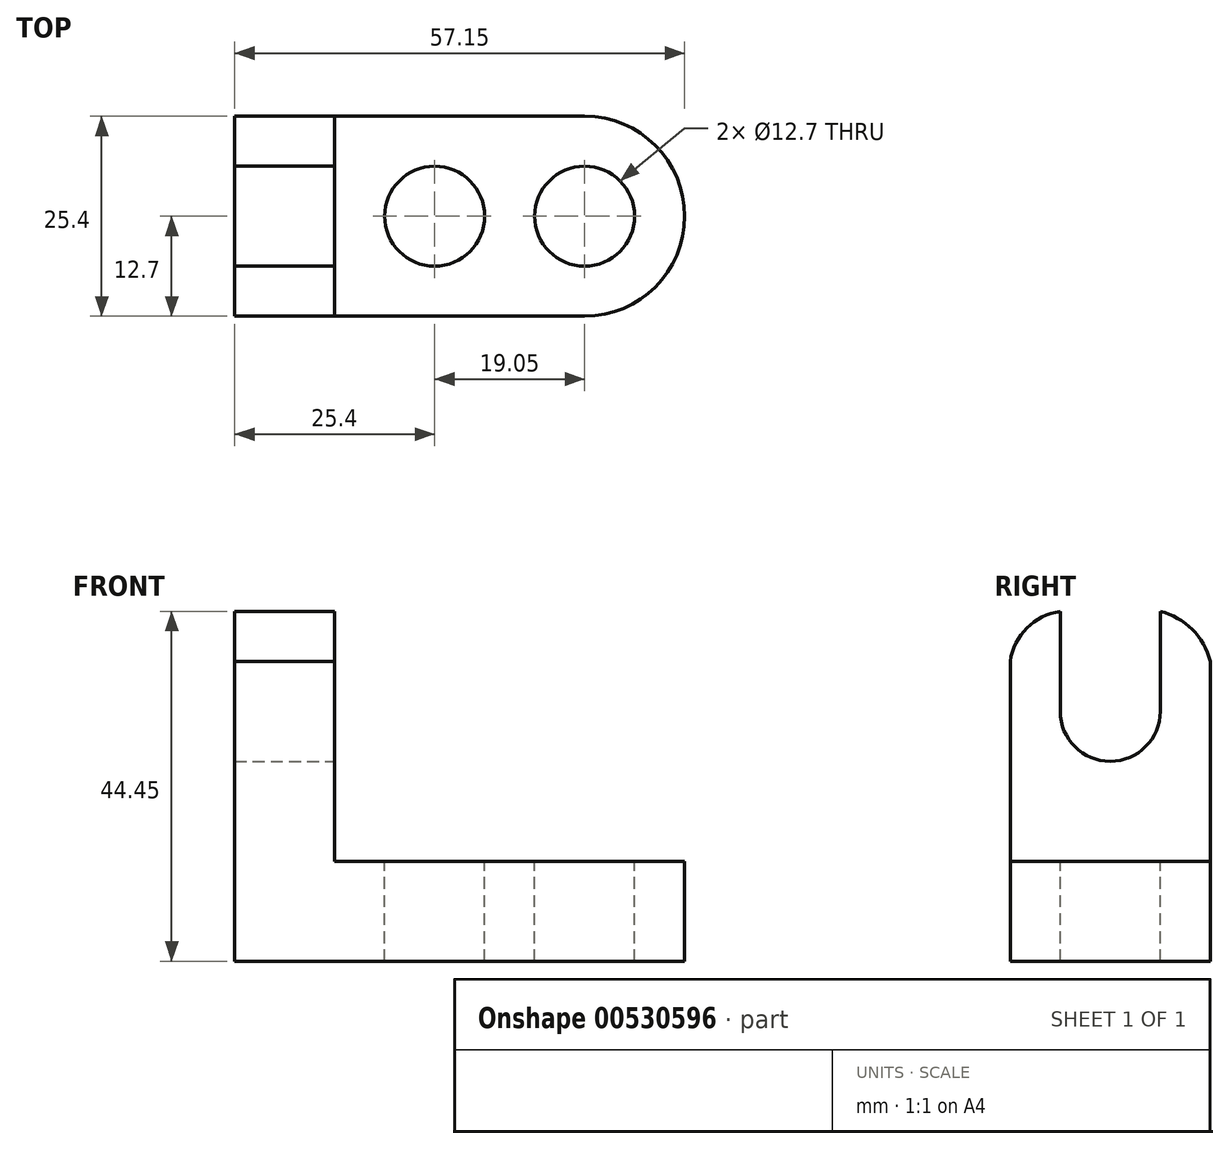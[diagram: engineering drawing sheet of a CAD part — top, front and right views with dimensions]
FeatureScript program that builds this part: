
annotation { "Feature Type Name" : "Feature", "Feature Type Description" : "" }
export const myFeature = defineFeature(function(context is Context, id is Id, definition is map)
    precondition{}
    {
        {
            var Q0;
            Q0=qCreatedBy(makeId("Front.planeOp"),FACE);
            var sketch = newSketch(context, id + "F0", { "sketchPlane" : qUnion([Q0])});
            skLineSegment(sketch, "E0", {"start": v(0, 0) * mm, "end": v(-44.45, 0) * mm});
            skLineSegment(sketch, "E1", {"start": v(-44.45, 0) * mm, "end": v(-44.45, 12.7) * mm});
            skLineSegment(sketch, "E2", {"start": v(-44.45, 12.7) * mm, "end": v(0, 12.7) * mm});
            skLineSegment(sketch, "E3", {"start": v(0, 12.7) * mm, "end": v(0, 0) * mm});
            skSolve(sketch);
        }
        {
            var Q0;
            Q0 = qSketchRegion(id + "F0", true);
            extrude(context, id + "F1", {"entities" : qUnion([Q0]), "depth" : 25.4 * mm, "offsetDistance" : 25.4 * mm});
        }
        {
            var Q0;
            Q0=makeQuery(id+"F1.opExtrude","SWEPT_FACE",FACE,{"disambiguationData":[OSD([sQuery(id+"F0.wireOp",EDGE,"E2")])]});
            var sketch = newSketch(context, id + "F2", { "sketchPlane" : qUnion([Q0])});
            skArc(sketch, "E4", {"start": v(0, -25.4) * mm, "mid": v(12.7, -12.7) * mm, "end": v(0, 0) * mm});
            skSolve(sketch);
        }
        {
            var Q0;
            Q0 = qSketchRegion(id + "F2", true);
            var Q1;
            Q1=makeQuery(id+"F2.imprint","IMPRINT",FACE,{"disambiguationData":[TD([[makeQuery(id+"F2.imprint","IMPRINT",EDGE,{"derivedFrom":sQuery(id+"F2.wireOp",EDGE,"E4")}),1.0]])]});
            extrude(context, id + "F3", {"entities" : qUnion([Q0, Q1]), "operationType" : NewBodyOperationType.ADD, "oppositeDirection" : true, "depth" : 12.7 * mm, "offsetDistance" : 25.4 * mm});
        }
        {
            var Q0;
            {var subQ0=sQuery(id+"F0.wireOp",EDGE,"E2");Q0=makeQuery(id+"F3.boolean.opBoolean","MERGE",FACE,{"derivedFrom":[makeQuery(id+"F1.opExtrude","SWEPT_FACE",FACE,{"disambiguationData":[OSD([subQ0])]}),makeQuery(id+"F3.opExtrude","CAP_FACE",FACE,{"disambiguationData":[OSD([subQ0,sQuery(id+"F0.wireOp",EDGE,"E3"),sQuery(id+"F2.wireOp",EDGE,"E4")])],"isStart":true})]});}
            var sketch = newSketch(context, id + "F4", { "sketchPlane" : qUnion([Q0])});
            skLineSegment(sketch, "E5", {"start": v(-44.45, 0) * mm, "end": v(-31.75, 0) * mm});
            skLineSegment(sketch, "E6", {"start": v(-31.75, 0) * mm, "end": v(-31.75, -25.4) * mm});
            skLineSegment(sketch, "E7", {"start": v(-31.75, -25.4) * mm, "end": v(-44.45, -25.4) * mm});
            skLineSegment(sketch, "E8", {"start": v(-44.45, -25.4) * mm, "end": v(-44.45, 0) * mm});
            skSolve(sketch);
        }
        {
            var Q0;
            Q0=makeQuery(id+"F4.imprint","IMPRINT",FACE,{"disambiguationData":[TD([[makeQuery(id+"F4.imprint","IMPRINT",EDGE,{"derivedFrom":sQuery(id+"F4.wireOp",EDGE,"E5")}),-1.0]])]});
            extrude(context, id + "F5", {"entities" : qUnion([Q0]), "operationType" : NewBodyOperationType.ADD, "depth" : 31.75 * mm, "offsetDistance" : 25.4 * mm});
        }
        {
            var Q0;
            Q0=makeQuery(id+"F5.opExtrude","SWEPT_FACE",FACE,{"disambiguationData":[OSD([sQuery(id+"F4.wireOp",EDGE,"E6")])]});
            var sketch = newSketch(context, id + "F6", { "sketchPlane" : qUnion([Q0])});
            skArc(sketch, "E9", {"start": v(-19.05, 44.45) * mm, "mid": v(-23.29, 42.34) * mm, "end": v(-25.4, 38.1) * mm});
            skArc(sketch, "E10", {"start": v(0, 38.1) * mm, "mid": v(-2.28, 42.17) * mm, "end": v(-6.35, 44.45) * mm});
            skSolve(sketch);
        }
        {
            var Q0;
            Q0 = qSketchRegion(id + "F6", true);
            var Q1;
            {var subQ0=sQuery(id+"F6.wireOp",EDGE,"E9");Q1=makeQuery(id+"F6.imprint","IMPRINT",FACE,{"disambiguationData":[TD([[makeQuery(id+"F6.imprint","IMPRINT",EDGE,{"derivedFrom":subQ0}),-1.0]])]});}
            var Q2;
            {var subQ0=sQuery(id+"F6.wireOp",EDGE,"E10");Q2=makeQuery(id+"F6.imprint","IMPRINT",FACE,{"disambiguationData":[TD([[makeQuery(id+"F6.imprint","IMPRINT",EDGE,{"derivedFrom":subQ0}),-1.0]])]});}
            extrude(context, id + "F7", {"entities" : qUnion([Q0, Q1, Q2]), "operationType" : NewBodyOperationType.REMOVE, "oppositeDirection" : true, "depth" : 25.4 * mm, "offsetDistance" : 25.4 * mm});
        }
        {
            var Q0;
            Q0=makeQuery(id+"F5.opExtrude","SWEPT_FACE",FACE,{"disambiguationData":[OSD([sQuery(id+"F4.wireOp",EDGE,"E6")])]});
            var sketch = newSketch(context, id + "F8", { "sketchPlane" : qUnion([Q0])});
            skLineSegment(sketch, "E11", {"start": v(-19.05, 44.45) * mm, "end": v(-19.05, 31.75) * mm});
            skLineSegment(sketch, "E12", {"start": v(-19.05, 31.75) * mm, "end": v(-6.35, 31.75) * mm});
            skLineSegment(sketch, "E13", {"start": v(-6.35, 31.75) * mm, "end": v(-6.35, 44.45) * mm});
            skLineSegment(sketch, "E14", {"start": v(-6.35, 44.45) * mm, "end": v(-19.05, 44.45) * mm});
            skArc(sketch, "E15", {"start": v(-19.05, 31.75) * mm, "mid": v(-12.7, 25.4) * mm, "end": v(-6.35, 31.75) * mm});
            skSolve(sketch);
        }
        {
            var Q0;
            Q0 = qSketchRegion(id + "F8", true);
            extrude(context, id + "F9", {"entities" : qUnion([Q0]), "operationType" : NewBodyOperationType.REMOVE, "oppositeDirection" : true, "depth" : 25.4 * mm, "offsetDistance" : 25.4 * mm});
        }
        {
            var Q0;
            {var subQ0=sQuery(id+"F0.wireOp",EDGE,"E2");Q0=makeQuery(id+"F3.boolean.opBoolean","MERGE",FACE,{"derivedFrom":[makeQuery(id+"F1.opExtrude","SWEPT_FACE",FACE,{"disambiguationData":[OSD([subQ0])]}),makeQuery(id+"F3.opExtrude","CAP_FACE",FACE,{"disambiguationData":[OSD([subQ0,sQuery(id+"F0.wireOp",EDGE,"E3"),sQuery(id+"F2.wireOp",EDGE,"E4")])],"isStart":true})]});}
            var sketch = newSketch(context, id + "F10", { "sketchPlane" : qUnion([Q0])});
            skCircle(sketch, "E16", {"center": v(-19.05, -12.7) * mm, "radius": 6.35 * mm});
            skCircle(sketch, "E17", {"center": v(0, -12.7) * mm, "radius": 6.35 * mm});
            skSolve(sketch);
        }
        {
            var Q0;
            Q0=makeQuery(id+"F10.imprint","IMPRINT",FACE,{"disambiguationData":[TD([[makeQuery(id+"F10.imprint","IMPRINT",EDGE,{"derivedFrom":sQuery(id+"F10.wireOp",EDGE,"E17")}),1.0]])]});
            var Q1;
            Q1=makeQuery(id+"F10.imprint","IMPRINT",FACE,{"disambiguationData":[TD([[makeQuery(id+"F10.imprint","IMPRINT",EDGE,{"derivedFrom":sQuery(id+"F10.wireOp",EDGE,"E16")}),1.0]])]});
            extrude(context, id + "F11", {"entities" : qUnion([Q0, Q1]), "operationType" : NewBodyOperationType.REMOVE, "oppositeDirection" : true, "depth" : 25.4 * mm, "offsetDistance" : 25.4 * mm});
        }
    });
